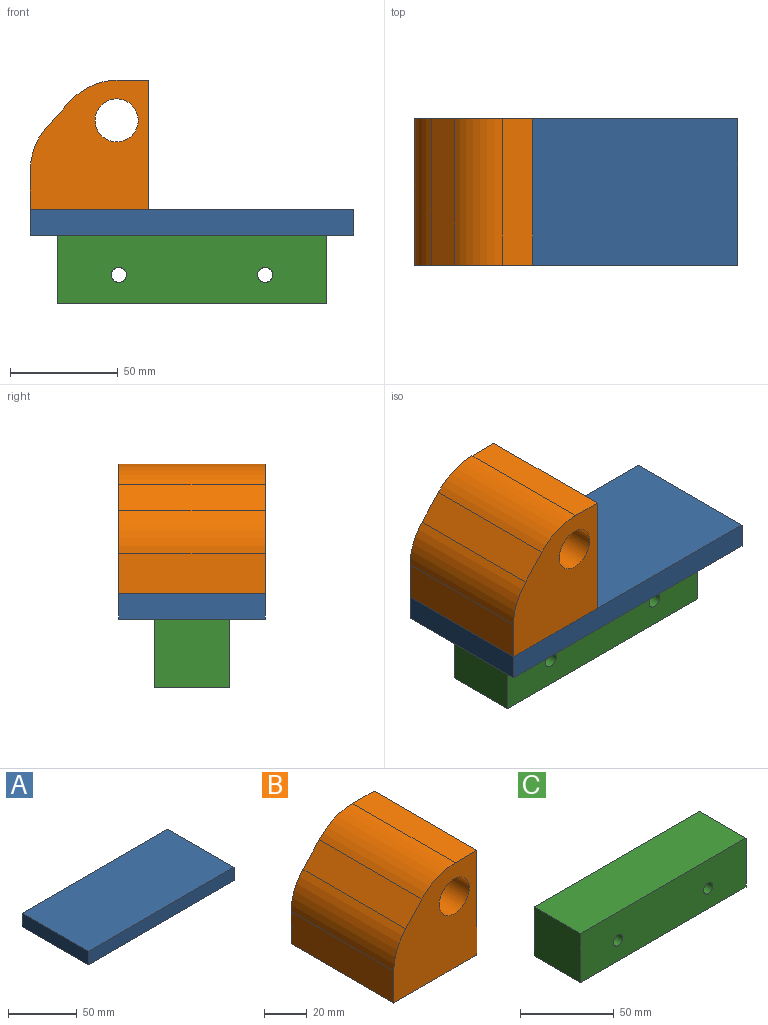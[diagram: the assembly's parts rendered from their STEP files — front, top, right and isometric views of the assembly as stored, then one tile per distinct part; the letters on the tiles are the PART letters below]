
ASSEMBLY  parts=3 mates=2
PART A: 6 faces, bbox 150x68x12 mm
  f0: plane 150x12mm, normal (0,1,0), area 1800mm2, adj f1,f3,f4,f5
  f1: plane 68x12mm, normal (-1,0,0), area 816mm2, adj f0,f2,f4,f5
  f2: plane 150x12mm, normal (0,-1,0), area 1800mm2, adj f1,f3,f4,f5
  f3: plane 68x12mm, normal (1,0,0), area 816mm2, adj f0,f2,f4,f5
  f4: plane 150x68mm, normal (0,0,1), area 10200mm2, adj f0,f1,f2,f3
  f5: plane 150x68mm, normal (0,0,-1), area 10200mm2, adj f0,f1,f2,f3
PART B: 10 faces, bbox 55x68x60 mm
  f0: plane 60x55mm, normal (0,1,0), area 2534.2mm2, adj f2,f3,f4,f5,f6,f7,f8,f9
  f1: plane 60x55mm, normal (0,-1,0), area 2534.2mm2, adj f2,f3,f4,f5,f6,f7,f8,f9
  f2: plane 68x18.33mm, normal (-1,0,0), area 1246.5mm2, adj f0,f1,f5,f8
  f3: plane 68x60mm, normal (1,0,0), area 4080mm2, adj f0,f1,f4,f5
  f4: plane 68x14.3mm, normal (0,0,1), area 972.6mm2, adj f0,f1,f3,f9
  f5: plane 68x55mm, normal (0,0,-1), area 3740mm2, adj f0,f1,f2,f3
  f6: plane 68x11.67mm, normal (-0.74,0,0.68), area 1076.5mm2, adj f0,f1,f8,f9
  f7: cylinder r=10mm len=68mm, axis (0,1,0), area 4272.6mm2, adj f0,f1
  f8: cylinder r=30mm len=68mm, axis (0,-1,0), area 1513.6mm2, adj f0,f1,f2,f6
  f9: cylinder r=30mm len=68mm, axis (0,1,0), area 1690.9mm2, adj f0,f1,f4,f6
PART C: 8 faces, bbox 125x35x32 mm
  f0: plane 125x35mm, normal (0,0,-1), area 4375mm2, adj f1,f4,f6,f7
  f1: plane 35x32mm, normal (1,0,0), area 1120mm2, adj f0,f2,f6,f7
  f2: plane 125x35mm, normal (0,0,1), area 4375mm2, adj f1,f4,f6,f7
  f3: cylinder r=3.5mm len=35mm, axis (0,1,0), area 769.7mm2, adj f6,f7
  f4: plane 35x32mm, normal (-1,0,0), area 1120mm2, adj f0,f2,f6,f7
  f5: cylinder r=3.5mm len=35mm, axis (0,1,0), area 769.7mm2, adj f6,f7
  f6: plane 125x32mm, normal (0,-1,0), area 3923mm2, adj f0,f1,f2,f3,f4,f5
  f7: plane 125x32mm, normal (0,1,0), area 3923mm2, adj f0,f1,f2,f3,f4,f5
PLACE A t=(-7.76,32.32,10.58)mm
PLACE B t=(62.24,16.7,22.58)mm
PLACE C t=(91.48,93.24,-21.42)mm
MATE fastened A.f4 <-> B.f5  axis (0,0,1) through (-46.02,41.74,22.58)mm
MATE fastened A.f5 <-> C.f2  axis (0,0,-1) through (28.98,75.74,10.58)mm
